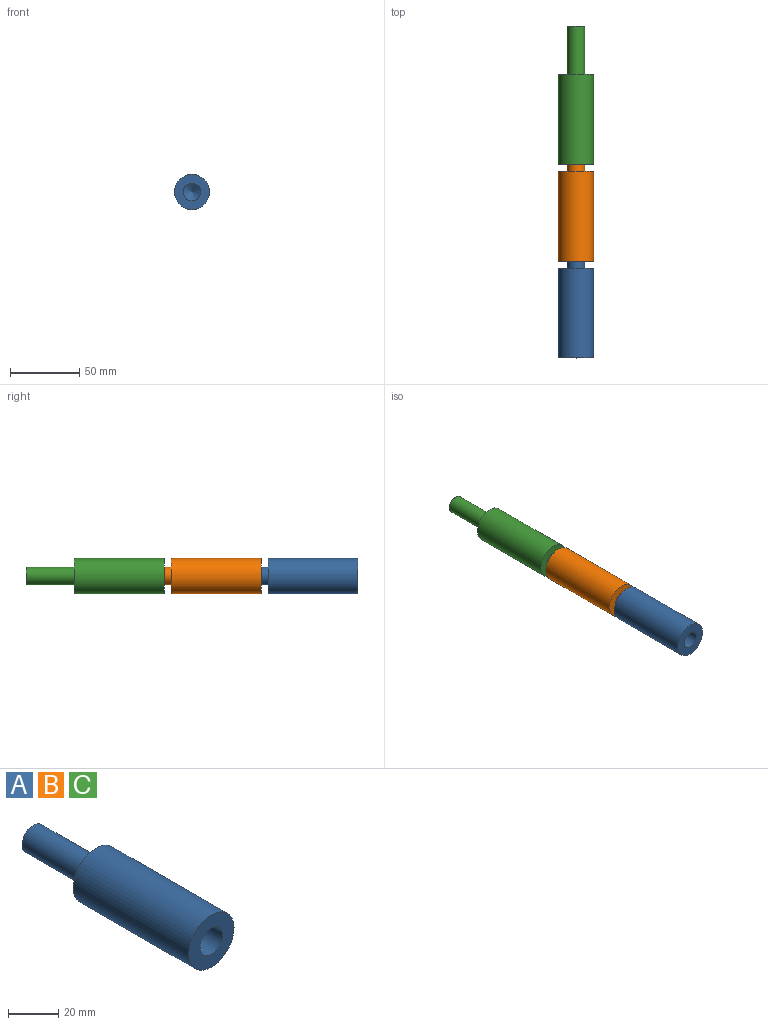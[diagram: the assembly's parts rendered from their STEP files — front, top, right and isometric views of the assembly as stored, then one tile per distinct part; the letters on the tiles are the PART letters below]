
ASSEMBLY  parts=3 mates=2
PART A: 7 faces, bbox 25.4x100x25.4 mm
  f0: cylinder r=12.7mm len=65mm, axis (0,1,0), area 5186.8mm2, adj f1,f2
  f1: plane 25.4x25.4mm, normal (0,-1,0), area 380mm2, adj f0,f6
  f2: plane 25.4x25.4mm, normal (0,1,0), area 380mm2, adj f0,f3
  f3: cylinder r=6.35mm len=35mm, axis (0,-1,0), area 1396.4mm2, adj f2,f4
  f4: plane 12.7x12.7mm, normal (0,1,0), area 126.7mm2, adj f3
  f5: cone r=0mm half-angle=59deg, axis (0,-1,0), area 147.8mm2, adj f6
  f6: cylinder r=6.35mm len=36mm, axis (0,-1,0), area 1436.3mm2, adj f1,f5
PART B: same geometry as A
PART C: same geometry as A
PLACE A t=(-27.83,-115.47,-13.25)mm
PLACE B t=(-27.83,-45.47,-13.25)mm
PLACE C t=(-27.83,24.53,-13.25)mm
MATE parallel A.f0 <-> B.f0  axis (0,1,0) through (-27.83,-115.47,-13.25)mm
MATE parallel B.f0 <-> C.f0  axis (0,1,0) through (-27.83,-45.47,-13.25)mm
